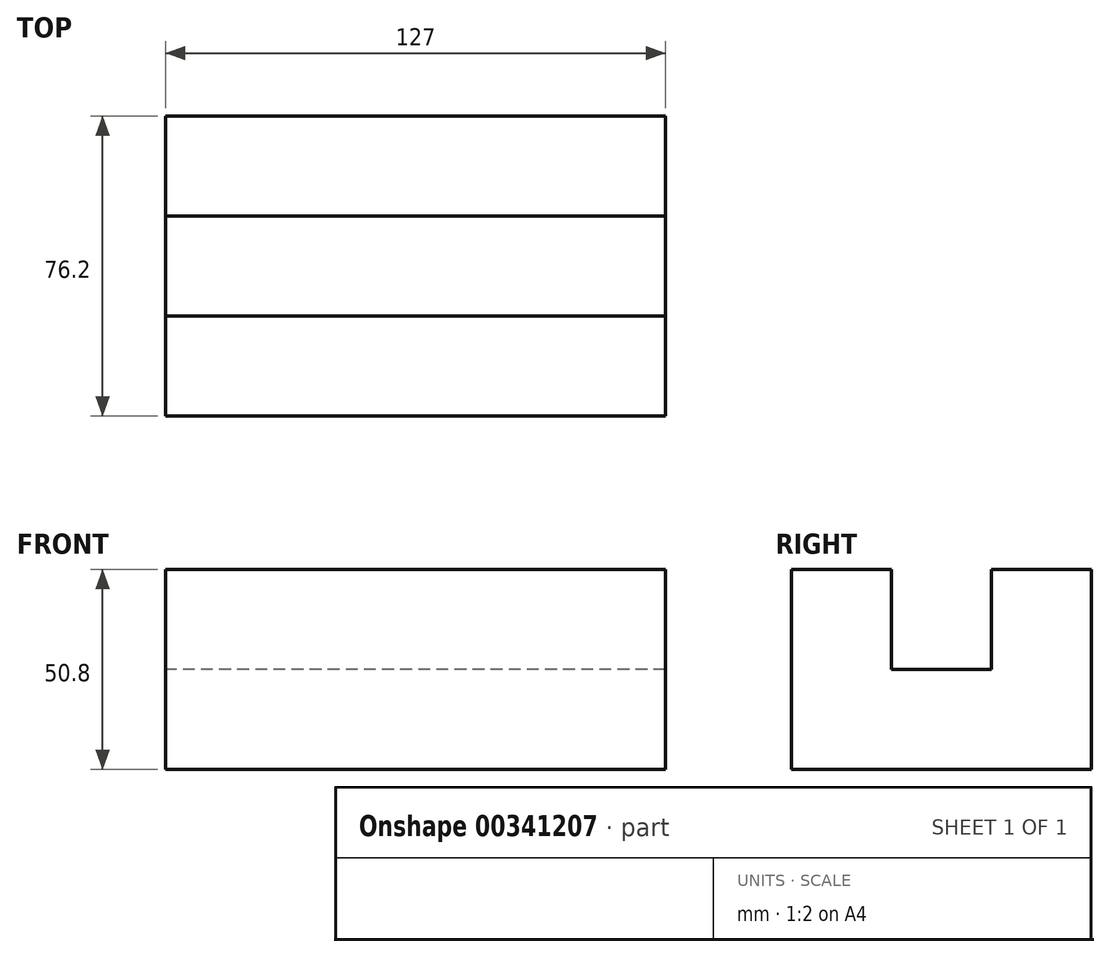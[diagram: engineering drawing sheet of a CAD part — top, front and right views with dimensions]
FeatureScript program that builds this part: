
annotation { "Feature Type Name" : "Feature", "Feature Type Description" : "" }
export const myFeature = defineFeature(function(context is Context, id is Id, definition is map)
    precondition{}
    {
        {
            var Q0;
            Q0=qCreatedBy(makeId("Right.planeOp"),FACE);
            var sketch = newSketch(context, id + "F0", { "sketchPlane" : qUnion([Q0])});
            skLineSegment(sketch, "E0", {"start": v(0, 0) * mm, "end": v(0, 50.8) * mm});
            skLineSegment(sketch, "E1", {"start": v(0, 50.8) * mm, "end": v(25.4, 50.8) * mm});
            skLineSegment(sketch, "E2", {"start": v(25.4, 50.8) * mm, "end": v(25.4, 25.4) * mm});
            skLineSegment(sketch, "E3", {"start": v(25.4, 25.4) * mm, "end": v(50.8, 25.4) * mm});
            skLineSegment(sketch, "E4", {"start": v(50.8, 25.4) * mm, "end": v(50.8, 50.8) * mm});
            skLineSegment(sketch, "E5", {"start": v(50.8, 50.8) * mm, "end": v(76.2, 50.8) * mm});
            skLineSegment(sketch, "E6", {"start": v(76.2, 50.8) * mm, "end": v(76.2, 0) * mm});
            skLineSegment(sketch, "E7", {"start": v(76.2, 0) * mm, "end": v(0, 0) * mm});
            skSolve(sketch);
        }
        {
            var Q0;
            Q0 = qSketchRegion(id + "F0", true);
            extrude(context, id + "F1", {"entities" : qUnion([Q0]), "depth" : 127 * mm});
        }
    });
